# Revit family: VL3_DN15-DN100_AMV(E) 438 SU_RFA_1
name_source: partatom
category: Pipe Accessories
units: mm (PartAtom-declared; Revit-internal decimal feet)

## family parameters
Always vertical = Yes
Cut with Voids When Loaded = No
OmniClass Number = 23.65.55.14.17
OmniClass Title = Adjusting/Controlling Valves for Liquid Services
Part Type = Valve - Breaks Into
Round Connector Dimension = Use Diameter
Shared = No
Work Plane-Based = No

## types (13) — shared parameters
082H0121 = AMV(E) 438 SU_RFA : AME 438 SU_24V_082H0121
082H0123 = AMV(E) 438 SU_RFA : AMV 438 SU_230V_082H0123
Actuator Type = AMV(E) 438 SU_RFA : AMV 438 SU_24V_082H0122
Adapter Type = Adapter_AMV(E)_RFA : Adapter_AMV(E) 15(25)(35)_DN15-50_065Z0311
Connection = Flange
Description = Motorized Control Valve
HB2 = 9 mm  [stored 0.0295276 ft]
HB2__ve = -9 mm  [stored -0.0295276 ft]
IfcExportAs = IfcValveType
IfcExportType = VL3
LOD 200 = No
LOD 350 = Yes
Manufacturer = Danfoss
Max Medium Temperature = 120 °C
Min Medium Temperature = 2 °C
Nominal Pressure = PN 6
Power = 12 VA
URL = https://store.danfoss.com
V100_LOD 200 = No
V_SMALL LOD 200 = No
Valve Body Material = Danfoss Grey Iron
Voltage = 24 V

## per-type parameters (varying)
- VL3_DN20_Kvs6.3_065Z0356: A1=3 mm  [stored 0.00984252 ft]; A1_Flow Pipe=172.00°; A2=47.12°; A2_Flow Pipe=165.00°; A3=15.00°; Adapter assembly=2 mm  [stored 0.00656168 ft]; Arc_100=10 mm  [stored 0.0328084 ft]; D=20 mm; DN15 to DN50=Yes; D_Connection End=52 mm; D_Flange=90 mm; Depth_Flange=14 mm  [stored 0.0459318 ft]; Depth_Flange_ve=-14 mm; EXT2=-54 mm  [stored -0.177165 ft]; EXT3=18 mm; Extrusion Bottom=54 mm; Extrusion Top=27 mm; Extrusion Top 2=8 mm  [stored 0.0262467 ft]; Flange Bottom Depth=14 mm  [stored 0.0459318 ft]; H1=33 mm; HB1=40 mm; HB1__ve=-40 mm  [stored -0.131234 ft]; HB3=3 mm  [stored 0.00984252 ft]; HE=0 mm  [stored 0 ft]; HE1=57 mm; HE1_100=3 mm  [stored 0.00984252 ft]; HE_100=0 mm  [stored 0 ft]; HH1=87 mm; HH2=70 mm; HR=28 mm; HR1=25 mm; Kvs=6.3 m³/h; L=150 mm; L1=3 mm  [stored 0.00984252 ft]; L1_ve=-3 mm  [stored -0.00984252 ft]; L2=75 mm; LE_100=30 mm; LV1=45 mm; LV2=9 mm  [stored 0.0295276 ft]; L_EXT=85 mm; L_S=48 mm; L_Top=3 mm  [stored 0.00984252 ft]; Model=065Z0356; Model Type=VL3_DN20_Kvs6.3; Offset Flow Pipe_1=6 mm  [stored 0.019685 ft]; Offset Flow Pipe_2=6 mm  [stored 0.019685 ft]; R1=23 mm; R1_1=20 mm; R1_1_1=20 mm; R1_2=13 mm  [stored 0.0426509 ft]; R1_Revolve=10 mm  [stored 0.0328084 ft]; R2_Revolve=8 mm  [stored 0.0262467 ft]; R3=24 mm; R3_2=27 mm; R_Flange Bottom=45 mm; R_Flow Pipe=17 mm; R_Top=13 mm  [stored 0.0426509 ft]; R_Vertical Body=18 mm; R_arc=35 mm; Stroke=10 mm; TH1=97 mm; V100=No; V_SMALL=Yes; W=138 mm; W2=20 mm; Weight=2.68 kg
- VL3_DN25_Kvs10_065Z0357: A1=5 mm  [stored 0.0164042 ft]; A1_Flow Pipe=169.00°; A2=47.12°; A2_Flow Pipe=165.00°; A3=10.00°; Adapter assembly=2 mm  [stored 0.00656168 ft]; Arc_100=10 mm  [stored 0.0328084 ft]; D=25 mm; DN15 to DN50=Yes; D_Connection End=62 mm; D_Flange=100 mm; Depth_Flange=14 mm  [stored 0.0459318 ft]; Depth_Flange_ve=-14 mm; EXT2=-58 mm  [stored -0.190289 ft]; EXT3=15 mm  [stored 0.0492126 ft]; Extrusion Bottom=62 mm; Extrusion Top=25 mm; Extrusion Top 2=5 mm  [stored 0.0164042 ft]; Flange Bottom Depth=15 mm  [stored 0.0492126 ft]; H1=37 mm; HB1=40 mm; HB1__ve=-40 mm  [stored -0.131234 ft]; HB3=3 mm  [stored 0.00984252 ft]; HE=0 mm  [stored 0 ft]; HE1=60 mm; HE1_100=3 mm  [stored 0.00984252 ft]; HE_100=0 mm  [stored 0 ft]; HH1=91 mm; HH2=75 mm; HR=31 mm; HR1=25 mm; Kvs=10.0 m³/h; L=160 mm; L1=3 mm  [stored 0.00984252 ft]; L1_ve=-3 mm  [stored -0.00984252 ft]; L2=80 mm; LE_100=30 mm; LV1=50 mm; LV2=12 mm  [stored 0.0393701 ft]; L_EXT=90 mm; L_S=48 mm; L_Top=3 mm  [stored 0.00984252 ft]; Model=065Z0357; Model Type=VL3_DN25_Kvs10; Offset Flow Pipe_1=9 mm  [stored 0.0295276 ft]; Offset Flow Pipe_2=6 mm  [stored 0.019685 ft]; R1=25 mm; R1_1=21 mm; R1_1_1=21 mm; R1_2=13 mm  [stored 0.0426509 ft]; R1_Revolve=12 mm  [stored 0.0393701 ft]; R2_Revolve=9 mm  [stored 0.0295276 ft]; R3=29 mm; R3_2=32 mm; R_Flange Bottom=50 mm; R_Flow Pipe=19 mm; R_Top=13 mm  [stored 0.0426509 ft]; R_Vertical Body=20 mm; R_arc=36 mm; Stroke=10 mm; TH1=101 mm; V100=No; V_SMALL=Yes; W=138 mm; W2=20 mm; Weight=3.59 kg
- VL3_DN32_Kvs16_065Z0358: A1=3 mm  [stored 0.00984252 ft]; A1_Flow Pipe=170.00°; A2=47.12°; A2_Flow Pipe=168.00°; A3=16.00°; Adapter assembly=1 mm  [stored 0.00328084 ft]; Arc_100=10 mm  [stored 0.0328084 ft]; D=32 mm; DN15 to DN50=Yes; D_Connection End=72 mm; D_Flange=120 mm; Depth_Flange=16 mm  [stored 0.0524934 ft]; Depth_Flange_ve=-16 mm  [stored -0.0524934 ft]; EXT2=-62 mm; EXT3=20 mm; Extrusion Bottom=73 mm; Extrusion Top=35 mm; Extrusion Top 2=10 mm  [stored 0.0328084 ft]; Flange Bottom Depth=16 mm  [stored 0.0524934 ft]; H1=42 mm; HB1=40 mm; HB1__ve=-40 mm  [stored -0.131234 ft]; HB3=3 mm  [stored 0.00984252 ft]; HE=0 mm  [stored 0 ft]; HE1=65 mm; HE1_100=3 mm  [stored 0.00984252 ft]; HE_100=0 mm  [stored 0 ft]; HH1=96 mm; HH2=80 mm; HR=31 mm; HR1=33 mm; Kvs=16.0 m³/h; L=180 mm; L1=3 mm  [stored 0.00984252 ft]; L1_ve=-3 mm  [stored -0.00984252 ft]; L2=90 mm; LE_100=30 mm; LV1=60 mm; LV2=13 mm  [stored 0.0426509 ft]; L_EXT=100 mm; L_S=48 mm; L_Top=3 mm  [stored 0.00984252 ft]; Model=065Z0358; Model Type=VL3_DN32_Kvs16; Offset Flow Pipe_1=7 mm  [stored 0.0229659 ft]; Offset Flow Pipe_2=9 mm  [stored 0.0295276 ft]; R1=29 mm; R1_1=24 mm; R1_1_1=24 mm; R1_2=13 mm  [stored 0.0426509 ft]; R1_Revolve=17 mm; R2_Revolve=14 mm  [stored 0.0459318 ft]; R3=35 mm; R3_2=37 mm; R_Flange Bottom=60 mm; R_Flow Pipe=24 mm; R_Top=13 mm  [stored 0.0426509 ft]; R_Vertical Body=25 mm; R_arc=41 mm; Stroke=15 mm; TH1=106 mm; V100=No; V_SMALL=Yes; W=138 mm; W2=26 mm; Weight=5.17 kg
- VL3_DN40_Kvs25_065Z0359: A1=3 mm  [stored 0.00984252 ft]; A1_Flow Pipe=168.00°; A2=47.12°; A2_Flow Pipe=166.00°; A3=15.00°; Adapter assembly=1 mm  [stored 0.00328084 ft]; Arc_100=10 mm  [stored 0.0328084 ft]; D=40 mm; DN15 to DN50=Yes; D_Connection End=82 mm; D_Flange=130 mm; Depth_Flange=16 mm  [stored 0.0524934 ft]; Depth_Flange_ve=-16 mm  [stored -0.0524934 ft]; EXT2=-72 mm; EXT3=30 mm; Extrusion Bottom=74 mm; Extrusion Top=37 mm; Extrusion Top 2=10 mm  [stored 0.0328084 ft]; Flange Bottom Depth=16 mm  [stored 0.0524934 ft]; H1=65 mm; HB1=40 mm; HB1__ve=-40 mm  [stored -0.131234 ft]; HB3=3 mm  [stored 0.00984252 ft]; HE=6 mm  [stored 0.019685 ft]; HE1=94 mm; HE1_100=3 mm  [stored 0.00984252 ft]; HE_100=0 mm  [stored 0 ft]; HH1=124 mm; HH2=90 mm; HR=40 mm; HR1=42 mm; Kvs=25.0 m³/h; L=200 mm; L1=3 mm  [stored 0.00984252 ft]; L1_ve=-3 mm  [stored -0.00984252 ft]; L2=100 mm; LE_100=30 mm; LV1=65 mm; LV2=9 mm  [stored 0.0295276 ft]; L_EXT=120 mm; L_S=48 mm; L_Top=3 mm  [stored 0.00984252 ft]; Model=065Z0359; Model Type=VL3_DN40_Kvs25; Offset Flow Pipe_1=11 mm  [stored 0.0360892 ft]; Offset Flow Pipe_2=10 mm  [stored 0.0328084 ft]; R1=36 mm; R1_1=29 mm; R1_1_1=29 mm; R1_2=20 mm; R1_Revolve=25 mm; R2_Revolve=23 mm; R3=39 mm; R3_2=42 mm; R_Flange Bottom=65 mm; R_Flow Pipe=28 mm; R_Top=13 mm  [stored 0.0426509 ft]; R_Vertical Body=29 mm; R_arc=50 mm; Stroke=15 mm; TH1=134 mm; V100=No; V_SMALL=Yes; W=130 mm; W2=31 mm; Weight=7.08 kg
- VL3_DN50_Kvs40_065Z0360: A1=1 mm  [stored 0.00328084 ft]; A1_Flow Pipe=165.00°; A2=47.12°; A2_Flow Pipe=168.00°; A3=20.00°; Adapter assembly=1 mm  [stored 0.00328084 ft]; Arc_100=10 mm  [stored 0.0328084 ft]; D=50 mm; DN15 to DN50=Yes; D_Connection End=93 mm; D_Flange=140 mm; Depth_Flange=17 mm; Depth_Flange_ve=-17 mm; EXT2=-80 mm  [stored -0.262467 ft]; EXT3=30 mm; Extrusion Bottom=83 mm; Extrusion Top=50 mm; Extrusion Top 2=10 mm  [stored 0.0328084 ft]; Flange Bottom Depth=17 mm; H1=77 mm; HB1=40 mm; HB1__ve=-40 mm  [stored -0.131234 ft]; HB3=3 mm  [stored 0.00984252 ft]; HE=6 mm  [stored 0.019685 ft]; HE1=106 mm; HE1_100=3 mm  [stored 0.00984252 ft]; HE_100=0 mm  [stored 0 ft]; HH1=137 mm; HH2=100 mm; HR=46 mm; HR1=55 mm; Kvs=40.0 m³/h; L=230 mm; L1=3 mm  [stored 0.00984252 ft]; L1_ve=-3 mm  [stored -0.00984252 ft]; L2=115 mm; LE_100=30 mm; LV1=70 mm; LV2=13 mm  [stored 0.0426509 ft]; L_EXT=150 mm; L_S=65 mm; L_Top=3 mm  [stored 0.00984252 ft]; Model=065Z0360; Model Type=VL3_DN50_Kvs40; Offset Flow Pipe_1=8 mm  [stored 0.0262467 ft]; Offset Flow Pipe_2=15 mm  [stored 0.0492126 ft]; R1=44 mm; R1_1=35 mm; R1_1_1=35 mm; R1_2=20 mm; R1_Revolve=33 mm; R2_Revolve=28 mm; R3=44 mm; R3_2=47 mm; R_Flange Bottom=70 mm; R_Flow Pipe=30 mm; R_Top=13 mm  [stored 0.0426509 ft]; R_Vertical Body=37 mm; R_arc=59 mm; Stroke=15 mm; TH1=147 mm; V100=No; V_SMALL=Yes; W=140 mm; W2=34 mm; Weight=10.11 kg
- VL3_DN65_Kvs63_065Z0361: A1=67 mm; A1_Flow Pipe=165.00°; A2=32.00°; A2_Flow Pipe=165.00°; A3=20.00°; Adapter assembly=5 mm  [stored 0.0164042 ft]; Arc_100=10 mm  [stored 0.0328084 ft]; D=65 mm; DN15 to DN50=No; D_Connection End=130 mm; D_Flange=186 mm; Depth_Flange=19 mm; Depth_Flange_ve=-19 mm  [stored -0.062336 ft]; EXT2=-98 mm  [stored -0.321522 ft]; EXT3=41 mm; Extrusion Bottom=98 mm; Extrusion Top=65 mm; Extrusion Top 2=20 mm; Flange Bottom Depth=20 mm; H1=84 mm; HB1=45 mm; HB1__ve=-45 mm  [stored -0.147638 ft]; HB3=5 mm  [stored 0.0164042 ft]; HE=7 mm  [stored 0.0229659 ft]; HE1=112 mm; HE1_100=3 mm  [stored 0.00984252 ft]; HE_100=0 mm  [stored 0 ft]; HH1=148 mm; HH2=122 mm; HR=58 mm; HR1=70 mm; Kvs=63.0 m³/h; L=290 mm; L1=6 mm  [stored 0.019685 ft]; L1_ve=-6 mm; L2=145 mm; LE_100=30 mm; LV1=150 mm; LV2=13 mm  [stored 0.0426509 ft]; L_EXT=185 mm; L_S=97 mm; L_Top=3 mm  [stored 0.00984252 ft]; Model=065Z0361; Model Type=VL3_DN65_Kvs63; Offset Flow Pipe_1=16 mm  [stored 0.0524934 ft]; Offset Flow Pipe_2=25 mm; R1=55 mm; R1_1=50 mm; R1_1_1=50 mm; R1_2=27 mm; R1_Revolve=48 mm; R2_Revolve=39 mm; R3=59 mm; R3_2=64 mm; R_Flange Bottom=93 mm; R_Flow Pipe=41 mm; R_Top=13 mm  [stored 0.0426509 ft]; R_Vertical Body=45 mm; R_arc=76 mm; Stroke=20 mm; TH1=158 mm; V100=No; V_SMALL=Yes; W=186 mm; W2=48 mm; Weight=16.15 kg
- VL3_DN80_Kvs100_065Z0362: A1=95 mm; A1_Flow Pipe=160.00°; A2=38.00°; A2_Flow Pipe=169.00°; A3=25.00°; Adapter assembly=5 mm  [stored 0.0164042 ft]; Arc_100=10 mm  [stored 0.0328084 ft]; D=80 mm; DN15 to DN50=No; D_Connection End=138 mm; D_Flange=200 mm; Depth_Flange=19 mm; Depth_Flange_ve=-19 mm  [stored -0.062336 ft]; EXT2=-133 mm  [stored -0.436352 ft]; EXT3=50 mm; Extrusion Bottom=133 mm; Extrusion Top=83 mm; Extrusion Top 2=20 mm; Flange Bottom Depth=20 mm; H1=100 mm; HB1=50 mm; HB1__ve=-50 mm  [stored -0.164042 ft]; HB3=6 mm  [stored 0.019685 ft]; HE=7 mm  [stored 0.0229659 ft]; HE1=128 mm; HE1_100=3 mm  [stored 0.00984252 ft]; HE_100=0 mm  [stored 0 ft]; HH1=164 mm; HH2=158 mm; HR=68 mm; HR1=70 mm; Kvs=100.0 m³/h; L=310 mm; L1=6 mm  [stored 0.019685 ft]; L1_ve=-6 mm; L2=155 mm; LE_100=30 mm; LV1=150 mm; LV2=13 mm  [stored 0.0426509 ft]; L_EXT=200 mm; L_S=95 mm; L_Top=3 mm  [stored 0.00984252 ft]; Model=065Z0362; Model Type=VL3_DN80_Kvs100; Offset Flow Pipe_1=25 mm; Offset Flow Pipe_2=21 mm; R1=63 mm; R1_1=56 mm; R1_1_1=55 mm; R1_2=27 mm; R1_Revolve=63 mm; R2_Revolve=50 mm; R3=64 mm; R3_2=69 mm; R_Flange Bottom=100 mm; R_Flow Pipe=44 mm; R_Top=13 mm  [stored 0.0426509 ft]; R_Vertical Body=55 mm; R_arc=94 mm; Stroke=20 mm; TH1=174 mm; V100=No; V_SMALL=Yes; W=200 mm; W2=55 mm; Weight=22.36 kg
- VL3_DN100_Kvs145_065Z3413: A1=43 mm; A1_Flow Pipe=165.00°; A2=44.00°; A2_Flow Pipe=166.00°; A3=0.00°; Adapter assembly=0 mm  [stored 0 ft]; Arc_100=30 mm; D=100 mm; DN15 to DN50=No; D_Connection End=160 mm; D_Flange=210 mm; Depth_Flange=20 mm; Depth_Flange_ve=-20 mm  [stored -0.0656168 ft]; EXT2=-155 mm  [stored -0.50853 ft]; EXT3=0 mm  [stored 0 ft]; Extrusion Bottom=152 mm; Extrusion Top=67 mm; Extrusion Top 2=20 mm; Flange Bottom Depth=21 mm; H1=78 mm; HB1=50 mm; HB1__ve=-50 mm  [stored -0.164042 ft]; HB3=4 mm  [stored 0.0131234 ft]; HE=0 mm  [stored 0 ft]; HE1=120 mm; HE1_100=73 mm; HE_100=-73 mm; HH1=132 mm; HH2=175 mm; HR=49 mm; HR1=75 mm; Kvs=145.0 m³/h; L=350 mm; L1=4 mm  [stored 0.0131234 ft]; L1_ve=-4 mm  [stored -0.0131234 ft]; L2=175 mm; LE_100=170 mm; LV1=150 mm; LV2=13 mm  [stored 0.0426509 ft]; L_EXT=19 mm; L_S=95 mm; L_Top=6 mm  [stored 0.019685 ft]; Model=065Z3413; Model Type=VL3_DN100_Kvs145; Offset Flow Pipe_1=24 mm; Offset Flow Pipe_2=33 mm; R1=17 mm; R1_1=59 mm; R1_1_1=35 mm; R1_2=17 mm; R1_Revolve=44 mm; R2_Revolve=38 mm; R3=77 mm; R3_2=81 mm; R_Flange Bottom=105 mm; R_Flow Pipe=48 mm; R_Top=18 mm; R_Vertical Body=70 mm; R_arc=94 mm; Stroke=30 mm; TH1=142 mm; V100=Yes; V_SMALL=No; W=210 mm; W2=35 mm; Weight=34.00 kg
- VL3_DN15_Kvs0.63_065Z0351: A1=3 mm  [stored 0.00984252 ft]; A1_Flow Pipe=170.00°; A2=47.12°; A2_Flow Pipe=166.00°; A3=13.00°; Adapter assembly=2 mm  [stored 0.00656168 ft]; Arc_100=10 mm  [stored 0.0328084 ft]; D=15 mm  [stored 0.0492126 ft]; DN15 to DN50=Yes; D_Connection End=42 mm; D_Flange=80 mm; Depth_Flange=12 mm  [stored 0.0393701 ft]; Depth_Flange_ve=-12 mm  [stored -0.0393701 ft]; EXT2=-50 mm  [stored -0.164042 ft]; EXT3=20 mm; Extrusion Bottom=49 mm; Extrusion Top=21 mm; Extrusion Top 2=5 mm  [stored 0.0164042 ft]; Flange Bottom Depth=12 mm  [stored 0.0393701 ft]; H1=31 mm; HB1=30 mm; HB1__ve=-30 mm  [stored -0.0984252 ft]; HB3=3 mm  [stored 0.00984252 ft]; HE=0 mm  [stored 0 ft]; HE1=54 mm; HE1_100=3 mm  [stored 0.00984252 ft]; HE_100=0 mm  [stored 0 ft]; HH1=85 mm; HH2=63 mm; HR=27 mm; HR1=23 mm; Kvs=0.6 m³/h; L=130 mm; L1=3 mm  [stored 0.00984252 ft]; L1_ve=-3 mm  [stored -0.00984252 ft]; L2=65 mm; LE_100=30 mm; LV1=40 mm; LV2=9 mm  [stored 0.0295276 ft]; L_EXT=80 mm; L_S=48 mm; L_Top=3 mm  [stored 0.00984252 ft]; Model=065Z0351; Model Type=VL3_DN15_Kvs0.63; Offset Flow Pipe_1=5 mm  [stored 0.0164042 ft]; Offset Flow Pipe_2=5 mm  [stored 0.0164042 ft]; R1=21 mm; R1_1=16 mm  [stored 0.0524934 ft]; R1_1_1=16 mm  [stored 0.0524934 ft]; R1_2=13 mm  [stored 0.0426509 ft]; R1_Revolve=9 mm  [stored 0.0295276 ft]; R2_Revolve=6 mm  [stored 0.019685 ft]; R3=19 mm; R3_2=22 mm; R_Flange Bottom=40 mm; R_Flow Pipe=15 mm  [stored 0.0492126 ft]; R_Top=13 mm  [stored 0.0426509 ft]; R_Vertical Body=16 mm  [stored 0.0524934 ft]; R_arc=30 mm; Stroke=10 mm; TH1=95 mm; V100=No; V_SMALL=Yes; W=138 mm; W2=16 mm  [stored 0.0524934 ft]; Weight=1.93 kg
- VL3_DN15_Kvs1.0_065Z0352: A1=3 mm  [stored 0.00984252 ft]; A1_Flow Pipe=170.00°; A2=47.12°; A2_Flow Pipe=166.00°; A3=13.00°; Adapter assembly=2 mm  [stored 0.00656168 ft]; Arc_100=10 mm  [stored 0.0328084 ft]; D=15 mm  [stored 0.0492126 ft]; DN15 to DN50=Yes; D_Connection End=42 mm; D_Flange=80 mm; Depth_Flange=12 mm  [stored 0.0393701 ft]; Depth_Flange_ve=-12 mm  [stored -0.0393701 ft]; EXT2=-50 mm  [stored -0.164042 ft]; EXT3=20 mm; Extrusion Bottom=49 mm; Extrusion Top=21 mm; Extrusion Top 2=5 mm  [stored 0.0164042 ft]; Flange Bottom Depth=12 mm  [stored 0.0393701 ft]; H1=31 mm; HB1=30 mm; HB1__ve=-30 mm  [stored -0.0984252 ft]; HB3=3 mm  [stored 0.00984252 ft]; HE=0 mm  [stored 0 ft]; HE1=54 mm; HE1_100=3 mm  [stored 0.00984252 ft]; HE_100=0 mm  [stored 0 ft]; HH1=85 mm; HH2=63 mm; HR=27 mm; HR1=23 mm; Kvs=1.0 m³/h; L=130 mm; L1=3 mm  [stored 0.00984252 ft]; L1_ve=-3 mm  [stored -0.00984252 ft]; L2=65 mm; LE_100=30 mm; LV1=40 mm; LV2=9 mm  [stored 0.0295276 ft]; L_EXT=80 mm; L_S=48 mm; L_Top=3 mm  [stored 0.00984252 ft]; Model=065Z0352; Model Type=VL3_DN15_Kvs1.0; Offset Flow Pipe_1=5 mm  [stored 0.0164042 ft]; Offset Flow Pipe_2=5 mm  [stored 0.0164042 ft]; R1=21 mm; R1_1=16 mm  [stored 0.0524934 ft]; R1_1_1=16 mm  [stored 0.0524934 ft]; R1_2=13 mm  [stored 0.0426509 ft]; R1_Revolve=9 mm  [stored 0.0295276 ft]; R2_Revolve=6 mm  [stored 0.019685 ft]; R3=19 mm; R3_2=22 mm; R_Flange Bottom=40 mm; R_Flow Pipe=15 mm  [stored 0.0492126 ft]; R_Top=13 mm  [stored 0.0426509 ft]; R_Vertical Body=16 mm  [stored 0.0524934 ft]; R_arc=30 mm; Stroke=10 mm; TH1=95 mm; V100=No; V_SMALL=Yes; W=138 mm; W2=16 mm  [stored 0.0524934 ft]; Weight=1.93 kg
- VL3_DN15_Kvs1.6_065Z0353: A1=3 mm  [stored 0.00984252 ft]; A1_Flow Pipe=170.00°; A2=47.12°; A2_Flow Pipe=166.00°; A3=13.00°; Adapter assembly=2 mm  [stored 0.00656168 ft]; Arc_100=10 mm  [stored 0.0328084 ft]; D=15 mm  [stored 0.0492126 ft]; DN15 to DN50=Yes; D_Connection End=42 mm; D_Flange=80 mm; Depth_Flange=12 mm  [stored 0.0393701 ft]; Depth_Flange_ve=-12 mm  [stored -0.0393701 ft]; EXT2=-50 mm  [stored -0.164042 ft]; EXT3=20 mm; Extrusion Bottom=49 mm; Extrusion Top=21 mm; Extrusion Top 2=5 mm  [stored 0.0164042 ft]; Flange Bottom Depth=12 mm  [stored 0.0393701 ft]; H1=31 mm; HB1=30 mm; HB1__ve=-30 mm  [stored -0.0984252 ft]; HB3=3 mm  [stored 0.00984252 ft]; HE=0 mm  [stored 0 ft]; HE1=54 mm; HE1_100=3 mm  [stored 0.00984252 ft]; HE_100=0 mm  [stored 0 ft]; HH1=85 mm; HH2=63 mm; HR=27 mm; HR1=23 mm; Kvs=1.6 m³/h; L=130 mm; L1=3 mm  [stored 0.00984252 ft]; L1_ve=-3 mm  [stored -0.00984252 ft]; L2=65 mm; LE_100=30 mm; LV1=40 mm; LV2=9 mm  [stored 0.0295276 ft]; L_EXT=80 mm; L_S=48 mm; L_Top=3 mm  [stored 0.00984252 ft]; Model=065Z0353; Model Type=VL3_DN15_Kvs1.6; Offset Flow Pipe_1=5 mm  [stored 0.0164042 ft]; Offset Flow Pipe_2=5 mm  [stored 0.0164042 ft]; R1=21 mm; R1_1=16 mm  [stored 0.0524934 ft]; R1_1_1=16 mm  [stored 0.0524934 ft]; R1_2=13 mm  [stored 0.0426509 ft]; R1_Revolve=9 mm  [stored 0.0295276 ft]; R2_Revolve=6 mm  [stored 0.019685 ft]; R3=19 mm; R3_2=22 mm; R_Flange Bottom=40 mm; R_Flow Pipe=15 mm  [stored 0.0492126 ft]; R_Top=13 mm  [stored 0.0426509 ft]; R_Vertical Body=16 mm  [stored 0.0524934 ft]; R_arc=30 mm; Stroke=10 mm; TH1=95 mm; V100=No; V_SMALL=Yes; W=138 mm; W2=16 mm  [stored 0.0524934 ft]; Weight=1.93 kg
- VL3_DN15_Kvs2.5_065Z0354: A1=3 mm  [stored 0.00984252 ft]; A1_Flow Pipe=170.00°; A2=47.12°; A2_Flow Pipe=166.00°; A3=13.00°; Adapter assembly=2 mm  [stored 0.00656168 ft]; Arc_100=10 mm  [stored 0.0328084 ft]; D=15 mm  [stored 0.0492126 ft]; DN15 to DN50=Yes; D_Connection End=42 mm; D_Flange=80 mm; Depth_Flange=12 mm  [stored 0.0393701 ft]; Depth_Flange_ve=-12 mm  [stored -0.0393701 ft]; EXT2=-50 mm  [stored -0.164042 ft]; EXT3=20 mm; Extrusion Bottom=49 mm; Extrusion Top=21 mm; Extrusion Top 2=5 mm  [stored 0.0164042 ft]; Flange Bottom Depth=12 mm  [stored 0.0393701 ft]; H1=31 mm; HB1=30 mm; HB1__ve=-30 mm  [stored -0.0984252 ft]; HB3=3 mm  [stored 0.00984252 ft]; HE=0 mm  [stored 0 ft]; HE1=54 mm; HE1_100=3 mm  [stored 0.00984252 ft]; HE_100=0 mm  [stored 0 ft]; HH1=85 mm; HH2=63 mm; HR=27 mm; HR1=23 mm; Kvs=2.5 m³/h; L=130 mm; L1=3 mm  [stored 0.00984252 ft]; L1_ve=-3 mm  [stored -0.00984252 ft]; L2=65 mm; LE_100=30 mm; LV1=40 mm; LV2=9 mm  [stored 0.0295276 ft]; L_EXT=80 mm; L_S=48 mm; L_Top=3 mm  [stored 0.00984252 ft]; Model=065Z0354; Model Type=VL3_DN15_Kvs2.5; Offset Flow Pipe_1=5 mm  [stored 0.0164042 ft]; Offset Flow Pipe_2=5 mm  [stored 0.0164042 ft]; R1=21 mm; R1_1=16 mm  [stored 0.0524934 ft]; R1_1_1=16 mm  [stored 0.0524934 ft]; R1_2=13 mm  [stored 0.0426509 ft]; R1_Revolve=9 mm  [stored 0.0295276 ft]; R2_Revolve=6 mm  [stored 0.019685 ft]; R3=19 mm; R3_2=22 mm; R_Flange Bottom=40 mm; R_Flow Pipe=15 mm  [stored 0.0492126 ft]; R_Top=13 mm  [stored 0.0426509 ft]; R_Vertical Body=16 mm  [stored 0.0524934 ft]; R_arc=30 mm; Stroke=10 mm; TH1=95 mm; V100=No; V_SMALL=Yes; W=138 mm; W2=16 mm  [stored 0.0524934 ft]; Weight=1.93 kg
- VL3_DN15_Kvs4.0_065Z0355: A1=3 mm  [stored 0.00984252 ft]; A1_Flow Pipe=170.00°; A2=47.12°; A2_Flow Pipe=166.00°; A3=13.00°; Adapter assembly=2 mm  [stored 0.00656168 ft]; Arc_100=10 mm  [stored 0.0328084 ft]; D=15 mm  [stored 0.0492126 ft]; DN15 to DN50=Yes; D_Connection End=42 mm; D_Flange=80 mm; Depth_Flange=12 mm  [stored 0.0393701 ft]; Depth_Flange_ve=-12 mm  [stored -0.0393701 ft]; EXT2=-50 mm  [stored -0.164042 ft]; EXT3=20 mm; Extrusion Bottom=49 mm; Extrusion Top=21 mm; Extrusion Top 2=5 mm  [stored 0.0164042 ft]; Flange Bottom Depth=12 mm  [stored 0.0393701 ft]; H1=31 mm; HB1=30 mm; HB1__ve=-30 mm  [stored -0.0984252 ft]; HB3=3 mm  [stored 0.00984252 ft]; HE=0 mm  [stored 0 ft]; HE1=54 mm; HE1_100=3 mm  [stored 0.00984252 ft]; HE_100=0 mm  [stored 0 ft]; HH1=85 mm; HH2=63 mm; HR=27 mm; HR1=23 mm; Kvs=4.0 m³/h; L=130 mm; L1=3 mm  [stored 0.00984252 ft]; L1_ve=-3 mm  [stored -0.00984252 ft]; L2=65 mm; LE_100=30 mm; LV1=40 mm; LV2=9 mm  [stored 0.0295276 ft]; L_EXT=80 mm; L_S=48 mm; L_Top=3 mm  [stored 0.00984252 ft]; Model=065Z0355; Model Type=VL3_DN15_Kvs4.0; Offset Flow Pipe_1=5 mm  [stored 0.0164042 ft]; Offset Flow Pipe_2=5 mm  [stored 0.0164042 ft]; R1=21 mm; R1_1=16 mm  [stored 0.0524934 ft]; R1_1_1=16 mm  [stored 0.0524934 ft]; R1_2=13 mm  [stored 0.0426509 ft]; R1_Revolve=9 mm  [stored 0.0295276 ft]; R2_Revolve=6 mm  [stored 0.019685 ft]; R3=19 mm; R3_2=22 mm; R_Flange Bottom=40 mm; R_Flow Pipe=15 mm  [stored 0.0492126 ft]; R_Top=13 mm  [stored 0.0426509 ft]; R_Vertical Body=16 mm  [stored 0.0524934 ft]; R_arc=30 mm; Stroke=10 mm; TH1=95 mm; V100=No; V_SMALL=Yes; W=138 mm; W2=16 mm  [stored 0.0524934 ft]; Weight=1.93 kg

note: [stored X ft] marks values corroborated as IEEE doubles in the binary element streams (Revit-internal decimal feet)

## geometry (parser evidence)
native form markers: Sweep x7
no freeform markers — native parametric forms only
